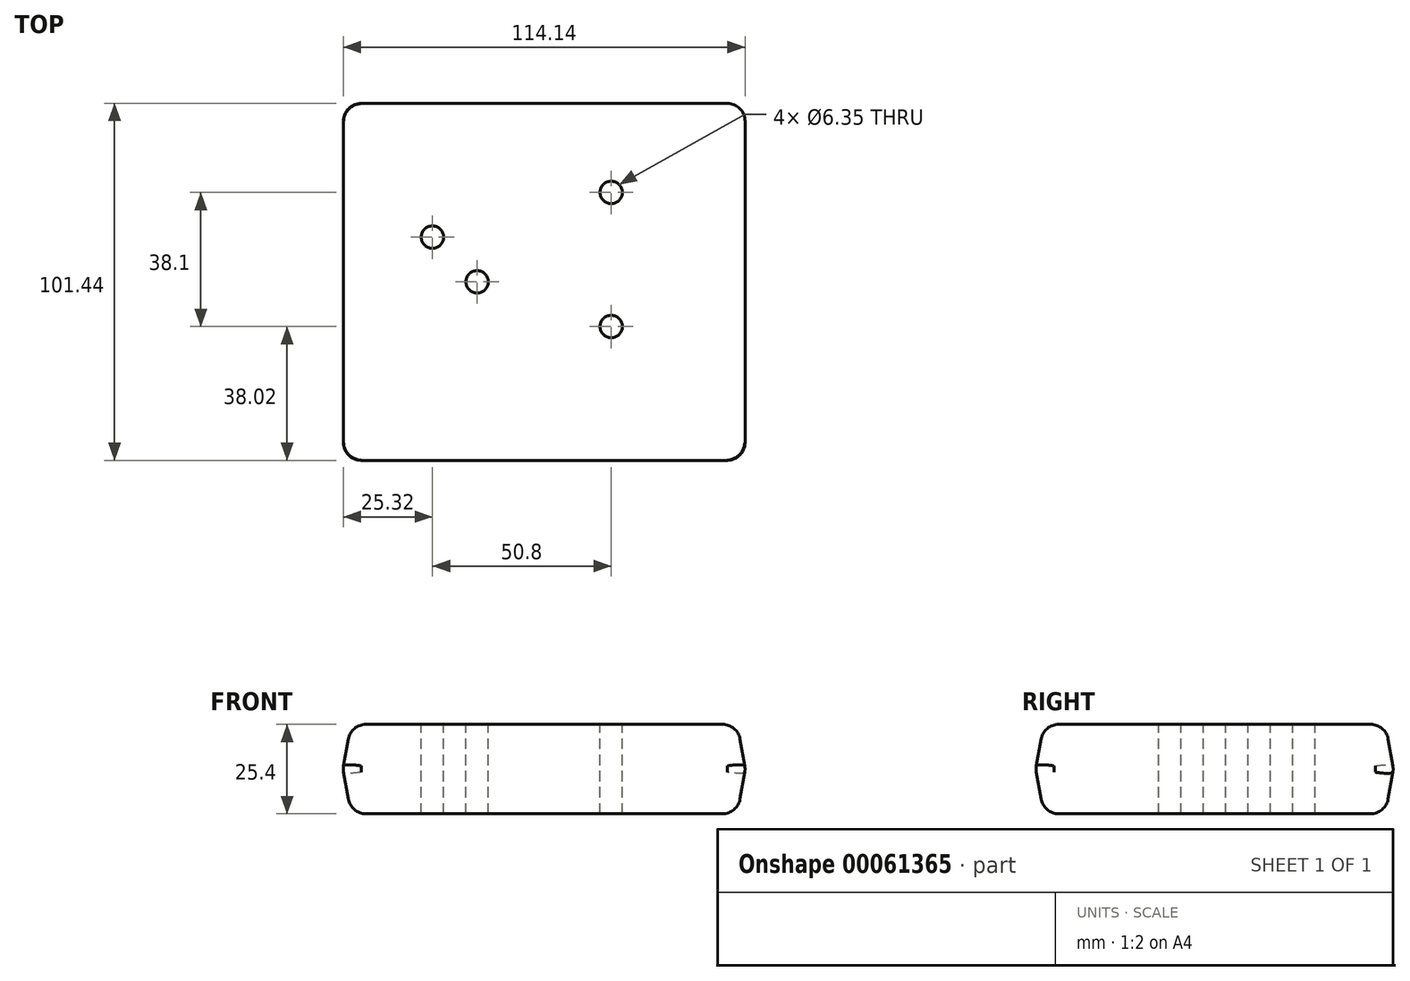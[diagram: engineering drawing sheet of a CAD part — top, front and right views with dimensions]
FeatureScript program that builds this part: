
annotation { "Feature Type Name" : "Feature", "Feature Type Description" : "" }
export const myFeature = defineFeature(function(context is Context, id is Id, definition is map)
    precondition{}
    {
        {
            var Q0;
            Q0=qCreatedBy(makeId("Top.planeOp"),FACE);
            var sketch = newSketch(context, id + "F0", { "sketchPlane" : qUnion([Q0])});
            skLineSegment(sketch, "E0.rect.bottom", {"start": v(57.15, 50.8) * mm, "end": v(-57.15, 50.8) * mm});
            skLineSegment(sketch, "E0.rect.top", {"start": v(57.15, -50.8) * mm, "end": v(-57.15, -50.8) * mm});
            skLineSegment(sketch, "E0.rect.left", {"start": v(57.15, 50.8) * mm, "end": v(57.15, -50.8) * mm});
            skLineSegment(sketch, "E0.rect.right", {"start": v(-57.15, 50.8) * mm, "end": v(-57.15, -50.8) * mm});
            skPoint(sketch, "E0.rect.middle", {"position": v(0, 0) * mm});
            skSolve(sketch);
        }
        {
            var Q0;
            Q0=makeQuery(id+"F0.imprint","IMPRINT",FACE,{"disambiguationData":[TD([[makeQuery(id+"F0.imprint","IMPRINT",EDGE,{"derivedFrom":sQuery(id+"F0.wireOp",EDGE,"E0.rect.bottom")}),1.0]])]});
            extrude(context, id + "F1", {"entities" : qUnion([Q0]), "endBound" : BoundingType.SYMMETRIC, "depth" : 25.4 * mm, "hasDraft" : true, "draftAngle" : 10 * degree, "draftPullDirection" : true});
        }
        {
            var Q0;
            Q0=makeQuery(id+"F1.opExtrude","CAP_EDGE",EDGE,{"disambiguationData":[OSD([sQuery(id+"F0.wireOp",EDGE,"E0.rect.top")])],"isStart":false});
            var Q1;
            Q1=makeQuery(id+"F1.opExtrude","CAP_EDGE",EDGE,{"disambiguationData":[OSD([sQuery(id+"F0.wireOp",EDGE,"E0.rect.left")])],"isStart":true});
            var Q2;
            Q2=makeQuery(id+"F1.opExtrude","CAP_EDGE",EDGE,{"disambiguationData":[OSD([sQuery(id+"F0.wireOp",EDGE,"E0.rect.left")])],"isStart":false});
            var Q3;
            Q3=makeQuery(id+"F1.*.split.splitOp","SPLIT",FACE,{"derivedFrom":makeQuery(id+"F1.opExtrude","SWEPT_FACE",FACE,{"disambiguationData":[OSD([sQuery(id+"F0.wireOp",EDGE,"E0.rect.top")])]}),"isFromBackBody":true});
            var Q4;
            Q4=makeQuery(id+"F1.opExtrude","CAP_FACE",FACE,{"disambiguationData":[OSD([sQuery(id+"F0.wireOp",EDGE,"E0.rect.bottom"),sQuery(id+"F0.wireOp",EDGE,"E0.rect.top"),sQuery(id+"F0.wireOp",EDGE,"E0.rect.left"),sQuery(id+"F0.wireOp",EDGE,"E0.rect.right")])],"isStart":false});
            var Q5;
            Q5=makeQuery(id+"F1.opExtrude","CAP_EDGE",EDGE,{"disambiguationData":[OSD([sQuery(id+"F0.wireOp",EDGE,"E0.rect.right")])],"isStart":false});
            var Q6;
            Q6=makeQuery(id+"F1.opExtrude","CAP_EDGE",EDGE,{"disambiguationData":[OSD([sQuery(id+"F0.wireOp",EDGE,"E0.rect.right")])],"isStart":true});
            var Q7;
            {var subQ0=makeQuery(id+"F1.opExtrude","SWEPT_FACE",FACE,{"disambiguationData":[OSD([sQuery(id+"F0.wireOp",EDGE,"E0.rect.right")])]});Q7=makeQuery(id+"F1.*.booleanUnion.opBoolean","MERGE",EDGE,{"derivedFrom":[makeQuery(id+"F1.*.split.splitOp","SPLIT_SURFACE_INTERSECT",EDGE,{"derivedFrom":[subQ0]}),makeQuery(id+"F1.*.split.splitOp","SPLIT_SURFACE_INTERSECT",EDGE,{"derivedFrom":[subQ0],"isFromBackBody":true})]});}
            var Q8;
            Q8=makeQuery(id+"F1.*.split.splitOp","SPLIT",EDGE,{"derivedFrom":makeQuery(id+"F1.opExtrude","SWEPT_EDGE",EDGE,{"disambiguationData":[OSD([sQuery(id+"F0.wireOp",EDGE,"E0.rect.top"),sQuery(id+"F0.wireOp",EDGE,"E0.rect.right")])]})});
            var Q9;
            Q9=makeQuery(id+"F1.*.split.splitOp","SPLIT",EDGE,{"derivedFrom":makeQuery(id+"F1.opExtrude","SWEPT_EDGE",EDGE,{"disambiguationData":[OSD([sQuery(id+"F0.wireOp",EDGE,"E0.rect.top"),sQuery(id+"F0.wireOp",EDGE,"E0.rect.left")])]})});
            var Q10;
            {var subQ0=makeQuery(id+"F1.opExtrude","SWEPT_FACE",FACE,{"disambiguationData":[OSD([sQuery(id+"F0.wireOp",EDGE,"E0.rect.left")])]});Q10=makeQuery(id+"F1.*.booleanUnion.opBoolean","MERGE",EDGE,{"derivedFrom":[makeQuery(id+"F1.*.split.splitOp","SPLIT_SURFACE_INTERSECT",EDGE,{"derivedFrom":[subQ0]}),makeQuery(id+"F1.*.split.splitOp","SPLIT_SURFACE_INTERSECT",EDGE,{"derivedFrom":[subQ0],"isFromBackBody":true})]});}
            var Q11;
            Q11=makeQuery(id+"F1.opExtrude","CAP_EDGE",EDGE,{"disambiguationData":[OSD([sQuery(id+"F0.wireOp",EDGE,"E0.rect.bottom")])],"isStart":true});
            var Q12;
            {var subQ0=makeQuery(id+"F1.opExtrude","SWEPT_FACE",FACE,{"disambiguationData":[OSD([sQuery(id+"F0.wireOp",EDGE,"E0.rect.bottom")])]});Q12=makeQuery(id+"F1.*.booleanUnion.opBoolean","MERGE",EDGE,{"derivedFrom":[makeQuery(id+"F1.*.split.splitOp","SPLIT_SURFACE_INTERSECT",EDGE,{"derivedFrom":[subQ0]}),makeQuery(id+"F1.*.split.splitOp","SPLIT_SURFACE_INTERSECT",EDGE,{"derivedFrom":[subQ0],"isFromBackBody":true})]});}
            var Q13;
            Q13=makeQuery(id+"F1.*.split.splitOp","SPLIT",EDGE,{"derivedFrom":makeQuery(id+"F1.opExtrude","SWEPT_EDGE",EDGE,{"disambiguationData":[OSD([sQuery(id+"F0.wireOp",EDGE,"E0.rect.bottom"),sQuery(id+"F0.wireOp",EDGE,"E0.rect.left")])]})});
            var Q14;
            Q14=makeQuery(id+"F1.*.split.splitOp","SPLIT",EDGE,{"derivedFrom":makeQuery(id+"F1.opExtrude","SWEPT_EDGE",EDGE,{"disambiguationData":[OSD([sQuery(id+"F0.wireOp",EDGE,"E0.rect.bottom"),sQuery(id+"F0.wireOp",EDGE,"E0.rect.left")])]}),"isFromBackBody":true});
            var Q15;
            Q15=makeQuery(id+"F1.*.split.splitOp","SPLIT",EDGE,{"derivedFrom":makeQuery(id+"F1.opExtrude","SWEPT_EDGE",EDGE,{"disambiguationData":[OSD([sQuery(id+"F0.wireOp",EDGE,"E0.rect.bottom"),sQuery(id+"F0.wireOp",EDGE,"E0.rect.right")])]})});
            var Q16;
            Q16=makeQuery(id+"F1.*.split.splitOp","SPLIT",EDGE,{"derivedFrom":makeQuery(id+"F1.opExtrude","SWEPT_EDGE",EDGE,{"disambiguationData":[OSD([sQuery(id+"F0.wireOp",EDGE,"E0.rect.bottom"),sQuery(id+"F0.wireOp",EDGE,"E0.rect.right")])]}),"isFromBackBody":true});
            fillet(context, id + "F2", {"entities" : qUnion([Q0, Q1, Q2, Q3, Q4, Q5, Q6, Q7, Q8, Q9, Q10, Q11, Q12, Q13, Q14, Q15, Q16]), "radius" : 5.08 * mm, "tangentPropagation" : true, "allowEdgeOverflow" : false});
        }
        {
            var Q0;
            Q0=makeQuery(id+"F1.opExtrude","CAP_FACE",FACE,{"disambiguationData":[OSD([sQuery(id+"F0.wireOp",EDGE,"E0.rect.bottom"),sQuery(id+"F0.wireOp",EDGE,"E0.rect.top"),sQuery(id+"F0.wireOp",EDGE,"E0.rect.left"),sQuery(id+"F0.wireOp",EDGE,"E0.rect.right")])],"isStart":false});
            var sketch = newSketch(context, id + "F3", { "sketchPlane" : qUnion([Q0])});
            skPoint(sketch, "E1", {"position": v(-19.05, 0) * mm});
            skPoint(sketch, "E2", {"position": v(19.05, -12.7) * mm});
            skPoint(sketch, "E3", {"position": v(-31.75, 12.7) * mm});
            skPoint(sketch, "E4", {"position": v(19.05, 25.4) * mm});
            skSolve(sketch);
        }
        {
            var Q0;
            Q0=sQuery(id+"F3.wireOp",VERTEX,"E1");
            var Q1;
            Q1=sQuery(id+"F3.wireOp",VERTEX,"E3");
            var Q2;
            Q2=sQuery(id+"F3.wireOp",VERTEX,"E4");
            var Q3;
            Q3=sQuery(id+"F3.wireOp",VERTEX,"E2");
            var Q4;
            Q4=makeQuery(id+"F1.*.split.splitOp","SPLIT",BODY,{"derivedFrom":makeQuery(id+"F1.opExtrude","SWEPT_BODY",BODY,{"disambiguationData":[OSD([sQuery(id+"F0.wireOp",EDGE,"E0.rect.bottom"),sQuery(id+"F0.wireOp",EDGE,"E0.rect.top"),sQuery(id+"F0.wireOp",EDGE,"E0.rect.left"),sQuery(id+"F0.wireOp",EDGE,"E0.rect.right")])]})});
            hole(context, id + "F4", {"style" : HoleStyle.SIMPLE, "holeDiameter" : 6.35 * mm, "endStyle" : HoleEndStyle.THROUGH, "locations" : qUnion([Q0, Q1, Q2, Q3]), "scope" : qUnion([Q4])});
        }
    });
